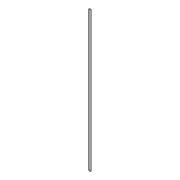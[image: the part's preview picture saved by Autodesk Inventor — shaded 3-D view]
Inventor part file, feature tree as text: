
AUTODESK INVENTOR PART (.ipt)
format: ipt  version: 2017 (Build 210142000, 142)  size: 91,136 bytes
history: native  units: mm
features: extrude x3, sketch x3
ambient origin geometry x8: Origin, YZ Plane, XZ Plane, XY Plane, X Axis, Y Axis, Z Axis, Center Point
bodies: Solid1 (feature_tree)
feature tree (6):
  extrude  "Extrusion1"  Depth=10.0mm
  extrude  "Extrusion2"  Depth=10.0mm TaperAngle=0.0deg
  extrude  "Extrusion3"  [1 undecoded]
  sketch  "Sketch1"  dims[d0=4.0mm d1=10.0mm]
  sketch  "Sketch2"  dims[d3=1950.0mm d4=0.0mm d5=10.0mm d6=0.0mm]
  sketch  "Sketch3"  dims[d7=10.0mm d8=0.0mm]
note: 1 required parameter value undecoded (feature->parameter linkage not recoverable at this tier; creation-order binding heuristic only, values carry confidence <= 0.55)
